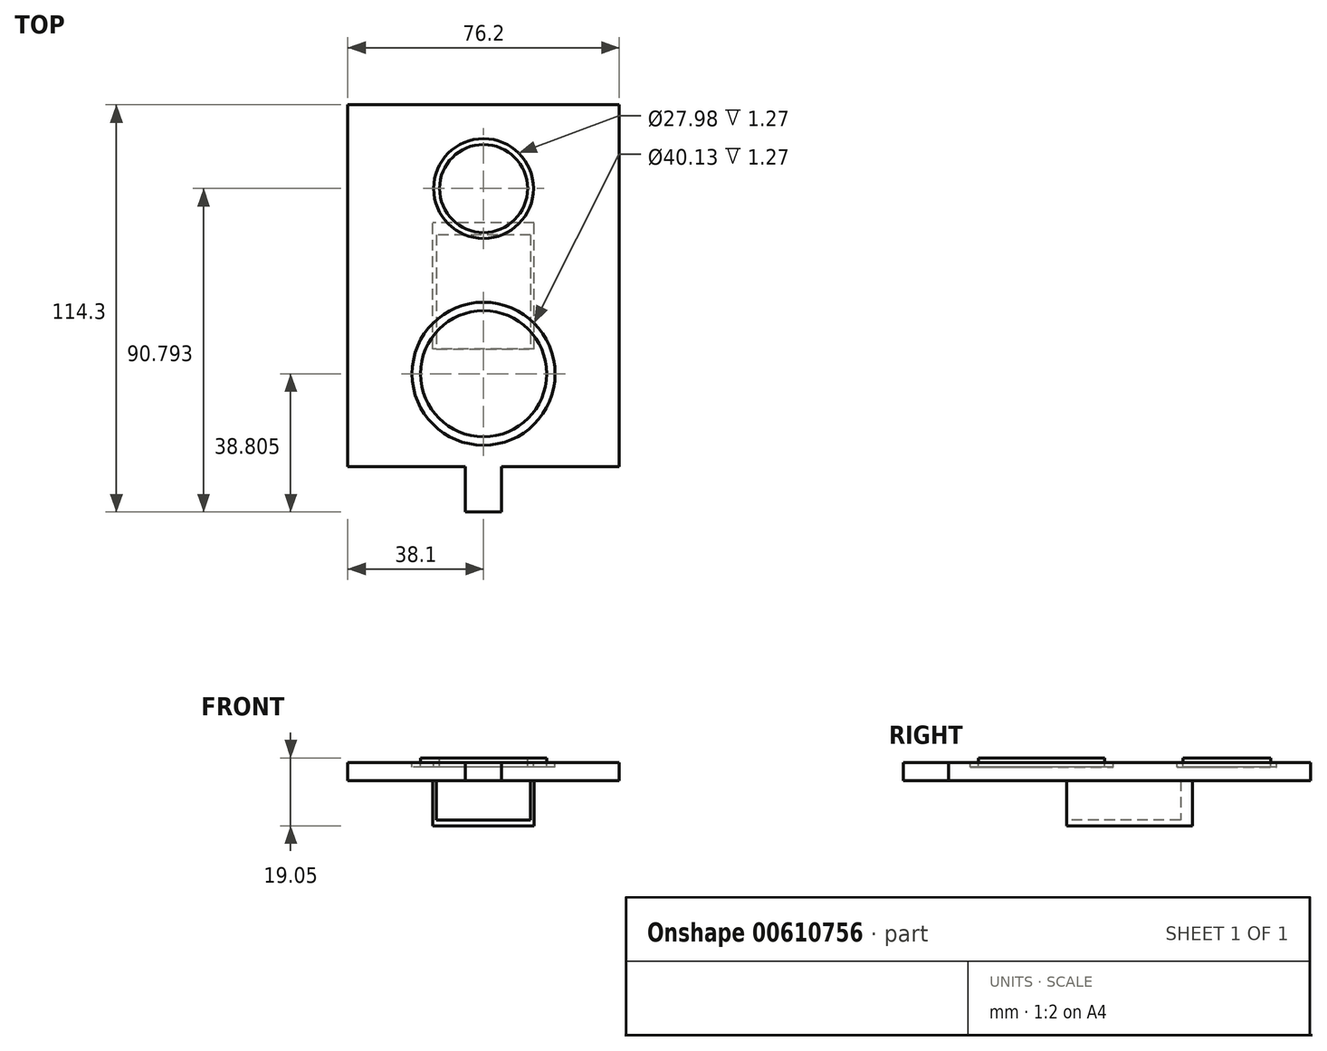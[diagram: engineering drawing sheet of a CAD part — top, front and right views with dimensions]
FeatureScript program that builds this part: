
annotation { "Feature Type Name" : "Feature", "Feature Type Description" : "" }
export const myFeature = defineFeature(function(context is Context, id is Id, definition is map)
    precondition{}
    {
        {
            var Q0;
            Q0=qCreatedBy(makeId("Top.planeOp"),FACE);
            var sketch = newSketch(context, id + "F0", { "sketchPlane" : qUnion([Q0])});
            skLineSegment(sketch, "E0.bottom", {"start": v(38.1, 50.8) * mm, "end": v(-38.1, 50.8) * mm});
            skLineSegment(sketch, "E0.top", {"start": v(38.1, -50.8) * mm, "end": v(-38.1, -50.8) * mm});
            skLineSegment(sketch, "E0.left", {"start": v(38.1, 50.8) * mm, "end": v(38.1, -50.8) * mm});
            skLineSegment(sketch, "E0.right", {"start": v(-38.1, 50.8) * mm, "end": v(-38.1, -50.8) * mm});
            skPoint(sketch, "E0.middle", {"position": v(0, 0) * mm});
            skSolve(sketch);
        }
        {
            var Q0;
            Q0 = qSketchRegion(id + "F0", true);
            extrude(context, id + "F1", {"entities" : qUnion([Q0]), "depth" : 5.08 * mm, "offsetDistance" : 25.4 * mm});
        }
        {
            var Q0;
            Q0=makeQuery(id+"F1.opExtrude","SWEPT_FACE",FACE,{"disambiguationData":[OSD([sQuery(id+"F0.wireOp",EDGE,"E0.top")])]});
            var sketch = newSketch(context, id + "F2", { "sketchPlane" : qUnion([Q0])});
            skLineSegment(sketch, "E1", {"start": v(0, 0) * mm, "end": v(-5.08, 0) * mm});
            skLineSegment(sketch, "E2", {"start": v(-5.08, 0) * mm, "end": v(-5.08, 5.08) * mm});
            skLineSegment(sketch, "E3", {"start": v(-5.08, 5.08) * mm, "end": v(5.08, 5.08) * mm});
            skLineSegment(sketch, "E4", {"start": v(5.08, 5.08) * mm, "end": v(5.08, 0) * mm});
            skLineSegment(sketch, "E5", {"start": v(5.08, 0) * mm, "end": v(0, 0) * mm});
            skSolve(sketch);
        }
        {
            var Q0;
            Q0 = qSketchRegion(id + "F2", true);
            extrude(context, id + "F3", {"entities" : qUnion([Q0]), "operationType" : NewBodyOperationType.ADD, "depth" : 12.7 * mm, "offsetDistance" : 25.4 * mm});
        }
        {
            var Q0;
            Q0=makeQuery(id+"F3.boolean.opBoolean","MERGE",FACE,{"derivedFrom":[makeQuery(id+"F1.opExtrude","CAP_FACE",FACE,{"disambiguationData":[OSD([sQuery(id+"F0.wireOp",EDGE,"E0.bottom"),sQuery(id+"F0.wireOp",EDGE,"E0.top"),sQuery(id+"F0.wireOp",EDGE,"E0.left"),sQuery(id+"F0.wireOp",EDGE,"E0.right")])],"isStart":true}),makeQuery(id+"F3.opExtrude","SWEPT_FACE",FACE,{"disambiguationData":[OSD([sQuery(id+"F2.wireOp",EDGE,"E1"),sQuery(id+"F2.wireOp",EDGE,"E5")])]})]});
            var sketch = newSketch(context, id + "F4", { "sketchPlane" : qUnion([Q0])});
            skLineSegment(sketch, "E6.bottom", {"start": v(16.54, 20.13) * mm, "end": v(-16.54, 20.13) * mm});
            skLineSegment(sketch, "E6.top", {"start": v(16.54, -20.13) * mm, "end": v(-16.54, -20.13) * mm});
            skLineSegment(sketch, "E6.left", {"start": v(16.54, 20.13) * mm, "end": v(16.54, -20.13) * mm});
            skLineSegment(sketch, "E6.right", {"start": v(-16.54, 20.13) * mm, "end": v(-16.54, -20.13) * mm});
            skPoint(sketch, "E6.middle", {"position": v(0, 0) * mm});
            skSolve(sketch);
        }
        {
            var Q0;
            Q0=makeQuery(id+"F4.imprint","IMPRINT",FACE,{"disambiguationData":[TD([[makeQuery(id+"F4.imprint","IMPRINT",EDGE,{"derivedFrom":sQuery(id+"F4.wireOp",EDGE,"E6.bottom")}),1.0]])]});
            var sketch = newSketch(context, id + "F5", { "sketchPlane" : qUnion([Q0])});
            skLineSegment(sketch, "E7.bottom", {"start": v(14.2, 17.7) * mm, "end": v(-14.2, 17.7) * mm});
            skLineSegment(sketch, "E7.top", {"start": v(14.2, -17.7) * mm, "end": v(-14.2, -17.7) * mm});
            skLineSegment(sketch, "E7.left", {"start": v(14.2, 17.7) * mm, "end": v(14.2, -17.7) * mm});
            skLineSegment(sketch, "E7.right", {"start": v(-14.2, 17.7) * mm, "end": v(-14.2, -17.7) * mm});
            skPoint(sketch, "E7.middle", {"position": v(0, 0) * mm});
            skSolve(sketch);
        }
        {
            var Q0;
            Q0 = qSketchRegion(id + "F5", true);
            extrude(context, id + "F6", {"entities" : qUnion([Q0]), "operationType" : NewBodyOperationType.ADD, "depth" : 12.7 * mm, "offsetDistance" : 25.4 * mm});
        }
        {
            var Q0;
            Q0=makeQuery(id+"F6.opExtrude","SWEPT_FACE",FACE,{"disambiguationData":[OSD([sQuery(id+"F5.wireOp",EDGE,"E7.bottom")])]});
            var sketch = newSketch(context, id + "F7", { "sketchPlane" : qUnion([Q0])});
            skLineSegment(sketch, "E8.bottom", {"start": v(-13.2, 0) * mm, "end": v(13.2, 0) * mm});
            skLineSegment(sketch, "E8.top", {"start": v(-13.2, -11.05) * mm, "end": v(13.2, -11.05) * mm});
            skLineSegment(sketch, "E8.left", {"start": v(-13.2, 0) * mm, "end": v(-13.2, -11.05) * mm});
            skLineSegment(sketch, "E8.right", {"start": v(13.2, 0) * mm, "end": v(13.2, -11.05) * mm});
            skPoint(sketch, "E8.middle", {"position": v(0, -5.53) * mm});
            skSolve(sketch);
        }
        {
            var Q0;
            Q0 = qSketchRegion(id + "F7", true);
            extrude(context, id + "F8", {"entities" : qUnion([Q0]), "operationType" : NewBodyOperationType.REMOVE, "oppositeDirection" : true, "depth" : 32 * mm, "offsetDistance" : 25.4 * mm});
        }
        {
            var Q0;
            Q0=makeQuery(id+"F3.boolean.opBoolean","MERGE",FACE,{"derivedFrom":[makeQuery(id+"F1.opExtrude","CAP_FACE",FACE,{"disambiguationData":[OSD([sQuery(id+"F0.wireOp",EDGE,"E0.bottom"),sQuery(id+"F0.wireOp",EDGE,"E0.top"),sQuery(id+"F0.wireOp",EDGE,"E0.left"),sQuery(id+"F0.wireOp",EDGE,"E0.right")])],"isStart":false}),makeQuery(id+"F3.opExtrude","SWEPT_FACE",FACE,{"disambiguationData":[OSD([sQuery(id+"F2.wireOp",EDGE,"E3")])]})]});
            var sketch = newSketch(context, id + "F9", { "sketchPlane" : qUnion([Q0])});
            skCircle(sketch, "E9", {"center": v(0, 27.3) * mm, "radius": 14 * mm});
            skCircle(sketch, "E10", {"center": v(0, -24.7) * mm, "radius": 20.07 * mm});
            skCircle(sketch, "E11", {"center": v(0, -24.7) * mm, "radius": 17.7 * mm});
            skCircle(sketch, "E12", {"center": v(0, 27.3) * mm, "radius": 12.35 * mm});
            skSolve(sketch);
        }
        {
            var Q0;
            Q0=makeQuery(id+"F9.imprint","IMPRINT",FACE,{"disambiguationData":[TD([[makeQuery(id+"F9.imprint","IMPRINT",EDGE,{"derivedFrom":sQuery(id+"F9.wireOp",EDGE,"E9")}),1.0]])]});
            var sketch = newSketch(context, id + "F10", { "sketchPlane" : qUnion([Q0])});
            skSolve(sketch);
        }
        {
            var Q0;
            Q0=makeQuery(id+"F9.imprint","IMPRINT",FACE,{"disambiguationData":[TD([[makeQuery(id+"F9.imprint","IMPRINT",EDGE,{"derivedFrom":sQuery(id+"F9.wireOp",EDGE,"E9")}),1.0]])]});
            extrude(context, id + "F11", {"entities" : qUnion([Q0]), "operationType" : NewBodyOperationType.REMOVE, "oppositeDirection" : true, "depth" : 1.27 * mm, "offsetDistance" : 25.4 * mm});
        }
        {
            var Q0;
            Q0=makeQuery(id+"F10.imprint","IMPRINT",FACE,{"disambiguationData":[TD([[makeQuery(id+"F10.imprint","IMPRINT",EDGE,{"derivedFrom":makeQuery(id+"F9.imprint","IMPRINT",EDGE,{"derivedFrom":sQuery(id+"F9.wireOp",EDGE,"E12")})}),1.0]])]});
            extrude(context, id + "F12", {"entities" : qUnion([Q0]), "operationType" : NewBodyOperationType.ADD, "depth" : 1.27 * mm, "offsetDistance" : 25.4 * mm});
        }
        {
            var Q0;
            Q0=makeQuery(id+"F9.imprint","IMPRINT",FACE,{"disambiguationData":[TD([[makeQuery(id+"F9.imprint","IMPRINT",EDGE,{"derivedFrom":sQuery(id+"F9.wireOp",EDGE,"E10")}),1.0]])]});
            extrude(context, id + "F13", {"entities" : qUnion([Q0]), "operationType" : NewBodyOperationType.REMOVE, "oppositeDirection" : true, "depth" : 1.27 * mm, "offsetDistance" : 25.4 * mm});
        }
        {
            var Q0;
            Q0=makeQuery(id+"F9.imprint","IMPRINT",FACE,{"disambiguationData":[TD([[makeQuery(id+"F9.imprint","IMPRINT",EDGE,{"derivedFrom":sQuery(id+"F9.wireOp",EDGE,"E11")}),1.0]])]});
            extrude(context, id + "F14", {"entities" : qUnion([Q0]), "operationType" : NewBodyOperationType.ADD, "depth" : 1.27 * mm, "offsetDistance" : 25.4 * mm});
        }
    });
